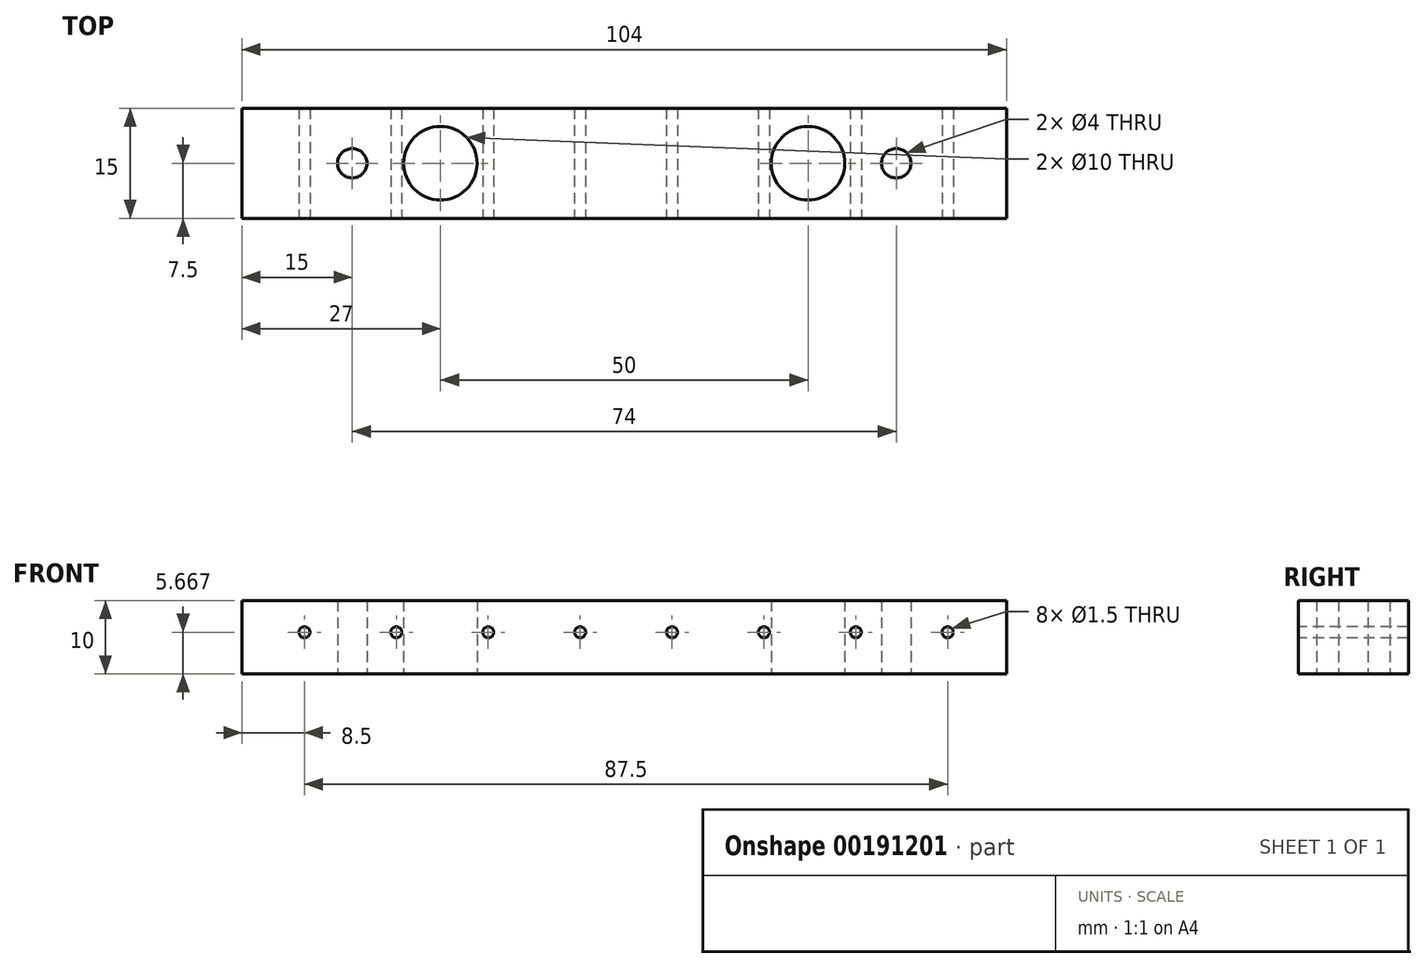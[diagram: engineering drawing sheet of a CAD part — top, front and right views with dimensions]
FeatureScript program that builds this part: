
annotation { "Feature Type Name" : "Feature", "Feature Type Description" : "" }
export const myFeature = defineFeature(function(context is Context, id is Id, definition is map)
    precondition{}
    {
        {
            var Q0;
            Q0=qCreatedBy(makeId("Top.planeOp"),FACE);
            var sketch = newSketch(context, id + "F0", { "sketchPlane" : qUnion([Q0])});
            skLineSegment(sketch, "E0.bottom", {"start": v(52, -7.5) * mm, "end": v(-52, -7.5) * mm});
            skLineSegment(sketch, "E0.top", {"start": v(52, 7.5) * mm, "end": v(-52, 7.5) * mm});
            skLineSegment(sketch, "E0.left", {"start": v(52, -7.5) * mm, "end": v(52, 7.5) * mm});
            skLineSegment(sketch, "E0.right", {"start": v(-52, -7.5) * mm, "end": v(-52, 7.5) * mm});
            skPoint(sketch, "E0.middle", {"position": v(0, 0) * mm});
            skCircle(sketch, "E1", {"center": v(-37, 0) * mm, "radius": 2 * mm});
            skPoint(sketch, "E2.centerSnap0", {"position": v(-52, 0) * mm});
            skCircle(sketch, "E3", {"center": v(37, 0) * mm, "radius": 2 * mm});
            skCircle(sketch, "E4", {"center": v(-25, 0) * mm, "radius": 5 * mm});
            skCircle(sketch, "E5", {"center": v(25, 0) * mm, "radius": 5 * mm});
            skSolve(sketch);
        }
        {
            var Q0;
            Q0=qSketchRegion(id+"F0",true);
            extrude(context, id + "F1", {"entities" : qUnion([Q0]), "depth" : 10 * mm});
        }
        {
            var Q0;
            Q0=makeQuery(id+"F1.opExtrude","SWEPT_FACE",FACE,{"disambiguationData":[OSD([sQuery(id+"F0.wireOp",EDGE,"E0.bottom")])]});
            var sketch = newSketch(context, id + "F2", { "sketchPlane" : qUnion([Q0])});
            skCircle(sketch, "E6", {"center": v(-43.5, 5.67) * mm, "radius": 0.75 * mm});
            skCircle(sketch, "E7.1.0.0", {"center": v(-31, 5.67) * mm, "radius": 0.75 * mm});
            skCircle(sketch, "E7.2.0.0", {"center": v(-18.5, 5.67) * mm, "radius": 0.75 * mm});
            skCircle(sketch, "E7.3.0.0", {"center": v(-6, 5.67) * mm, "radius": 0.75 * mm});
            skCircle(sketch, "E7.4.0.0", {"center": v(6.5, 5.67) * mm, "radius": 0.75 * mm});
            skCircle(sketch, "E7.5.0.0", {"center": v(19, 5.67) * mm, "radius": 0.75 * mm});
            skCircle(sketch, "E7.6.0.0", {"center": v(31.5, 5.67) * mm, "radius": 0.75 * mm});
            skCircle(sketch, "E7.7.0.0", {"center": v(44, 5.67) * mm, "radius": 0.75 * mm});
            skLineSegment(sketch, "E7.direction1", {"start": v(-43.5, 5.67) * mm, "end": v(-31, 5.67) * mm, "construction": true});
            skSolve(sketch);
        }
        {
            var Q0;
            Q0=qSketchRegion(id+"F2",true);
            extrude(context, id + "F3", {"entities" : qUnion([Q0]), "operationType" : NewBodyOperationType.REMOVE, "oppositeDirection" : true, "depth" : 25 * mm});
        }
    });
